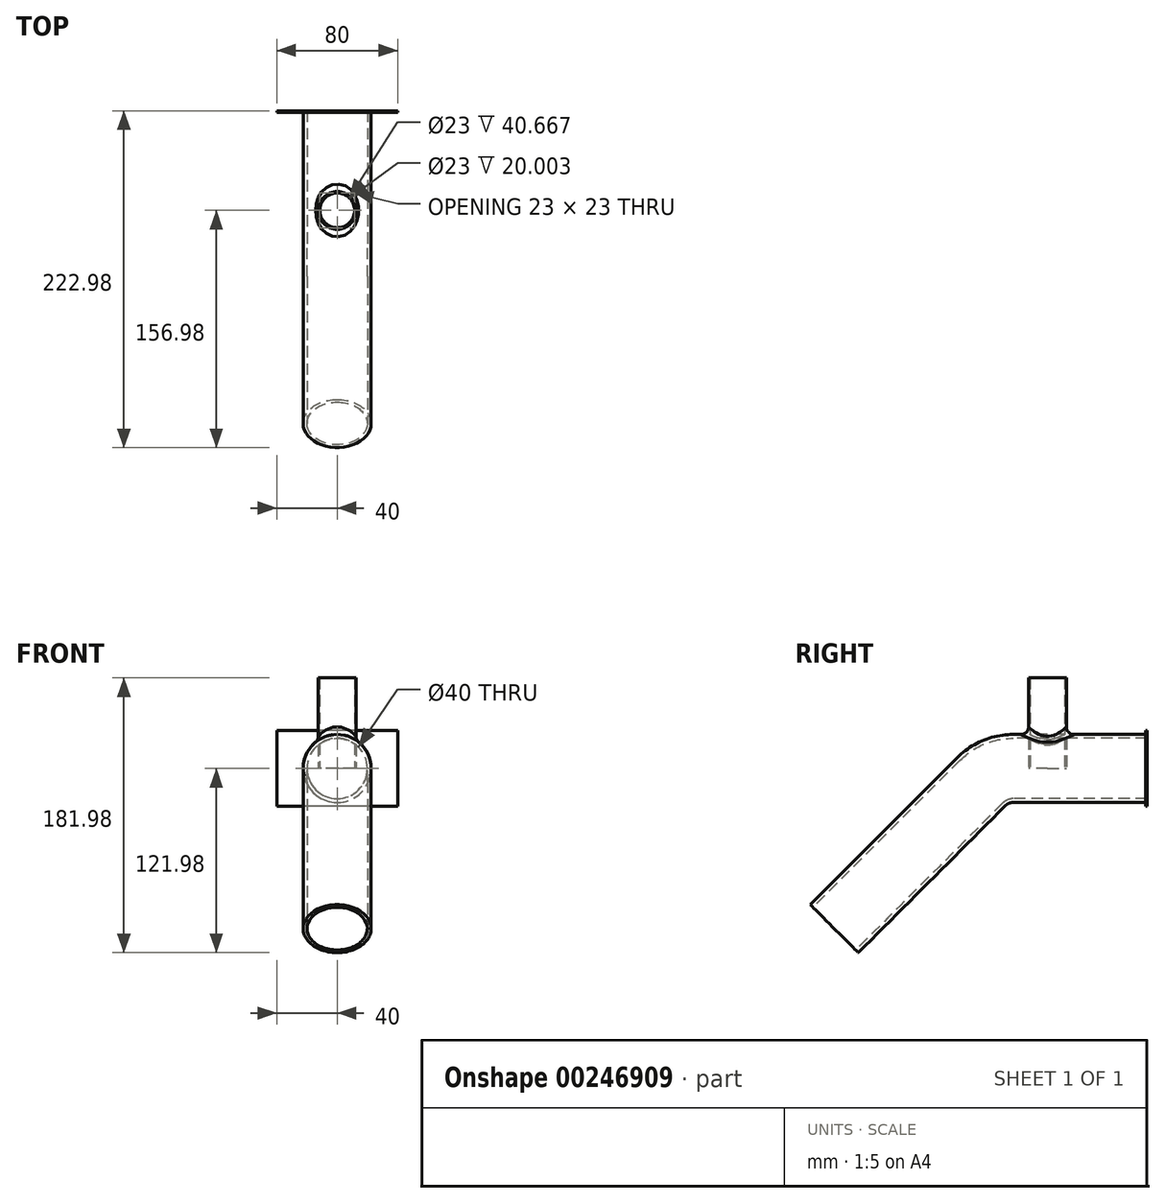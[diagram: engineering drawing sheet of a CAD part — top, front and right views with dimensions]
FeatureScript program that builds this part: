
annotation { "Feature Type Name" : "Feature", "Feature Type Description" : "" }
export const myFeature = defineFeature(function(context is Context, id is Id, definition is map)
    precondition{}
    {
        {
            var Q0;
            Q0=qCreatedBy(makeId("Front.planeOp"),FACE);
            var sketch = newSketch(context, id + "F0", { "sketchPlane" : qUnion([Q0])});
            skCircle(sketch, "E0", {"center": v(0, 0) * mm, "radius": 20 * mm});
            skLineSegment(sketch, "E1.bottom", {"start": v(40, 25) * mm, "end": v(-40, 25) * mm});
            skLineSegment(sketch, "E1.top", {"start": v(40, -25) * mm, "end": v(-40, -25) * mm});
            skLineSegment(sketch, "E1.left", {"start": v(40, 25) * mm, "end": v(40, -25) * mm});
            skLineSegment(sketch, "E1.right", {"start": v(-40, 25) * mm, "end": v(-40, -25) * mm});
            skSolve(sketch);
        }
        {
            var Q0;
            Q0 = qSketchRegion(id + "F0", true);
            extrude(context, id + "F1", {"entities" : qUnion([Q0]), "oppositeDirection" : true, "depth" : 1 * mm});
        }
        {
            var Q0;
            Q0=makeQuery(id+"F1.opExtrude","CAP_FACE",FACE,{"disambiguationData":[OSD([sQuery(id+"F0.wireOp",EDGE,"E0"),sQuery(id+"F0.wireOp",EDGE,"E1.bottom"),sQuery(id+"F0.wireOp",EDGE,"E1.top"),sQuery(id+"F0.wireOp",EDGE,"E1.left"),sQuery(id+"F0.wireOp",EDGE,"E1.right")])],"isStart":true});
            var sketch = newSketch(context, id + "F2", { "sketchPlane" : qUnion([Q0])});
            skCircle(sketch, "E2", {"center": v(0, 0) * mm, "radius": 22.5 * mm});
            skCircle(sketch, "E3", {"center": v(0, 0) * mm, "radius": 20 * mm});
            skSolve(sketch);
        }
        {
            var Q0;
            Q0=qCreatedBy(makeId("Right.planeOp"),FACE);
            var sketch = newSketch(context, id + "F3", { "sketchPlane" : qUnion([Q0])});
            skLineSegment(sketch, "E4", {"start": v(0, 0) * mm, "end": v(-87.57, 0) * mm});
            skLineSegment(sketch, "E5", {"start": v(-108.79, -8.79) * mm, "end": v(-206.07, -106.07) * mm});
            skPoint(sketch, "E6.visualSharp", {"position": v(-100, 0) * mm});
            skArc(sketch, "E6.filletArc", {"start": v(-87.57, 0) * mm, "mid": v(-99.05, -2.28) * mm, "end": v(-108.79, -8.79) * mm});
            skSolve(sketch);
        }
        {
            var Q0;
            Q0 = qSketchRegion(id + "F2", true);
            var Q1;
            Q1 = qConstructionFilter(qBodyType(qCreatedBy(id + "F3" ,EDGE), BodyType.WIRE), ConstructionObject.NO);
            sweep(context, id + "F4", {"operationType" : NewBodyOperationType.ADD, "profiles" : qUnion([Q0]), "path" : qUnion([Q1])});
        }
        {
            var Q0;
            Q0=qCreatedBy(makeId("Top.planeOp"),FACE);
            var sketch = newSketch(context, id + "F5", { "sketchPlane" : qUnion([Q0])});
            skCircle(sketch, "E7", {"center": v(0, -65) * mm, "radius": 12.5 * mm});
            skCircle(sketch, "E8", {"center": v(0, -65) * mm, "radius": 11.5 * mm});
            skSolve(sketch);
        }
        {
            var Q0;
            Q0 = qSketchRegion(id + "F5", true);
            extrude(context, id + "F6", {"entities" : qUnion([Q0]), "operationType" : NewBodyOperationType.ADD, "depth" : 60 * mm});
        }
        {
            var Q0;
            Q0=makeQuery(id+"F4.opSweep","CAP_EDGE",EDGE,{"disambiguationData":[OSD([sQuery(id+"F2.wireOp",EDGE,"E2"),sQuery(id+"F3.wireOp",VERTEX,"E4.start")])],"isStart":true});
            var Q1;
            Q1=makeQuery(id+"F6.boolean.opBoolean","INTERSECT",EDGE,{"derivedFrom":[makeQuery(id+"F4.opSweep","SWEPT_FACE",FACE,{"disambiguationData":[OSD([sQuery(id+"F2.wireOp",EDGE,"E2"),sQuery(id+"F3.wireOp",EDGE,"E4")])]}),makeQuery(id+"F6.opExtrude","SWEPT_FACE",FACE,{"disambiguationData":[OSD([sQuery(id+"F5.wireOp",EDGE,"E7")])]})]});
            fillet(context, id + "F7", {"entities" : qUnion([Q0, Q1]), "radius" : 5 * mm, "tangentPropagation" : true, "allowEdgeOverflow" : false});
        }
    });
